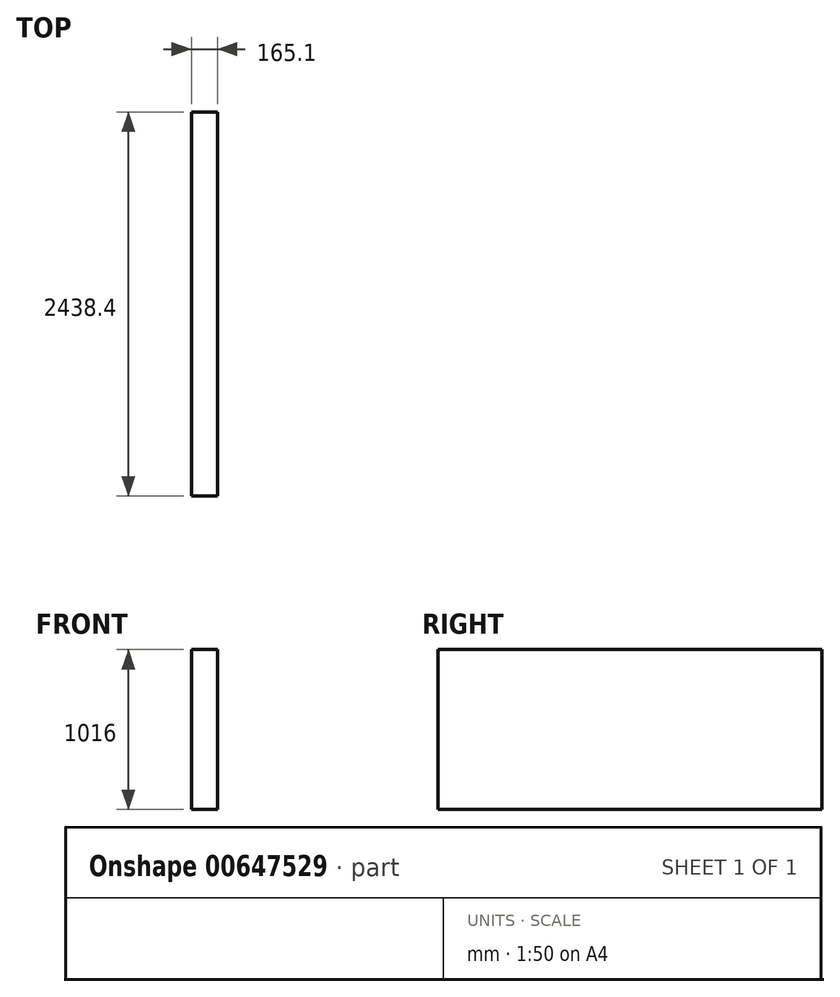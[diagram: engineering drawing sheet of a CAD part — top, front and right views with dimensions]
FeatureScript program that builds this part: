
annotation { "Feature Type Name" : "Feature", "Feature Type Description" : "" }
export const myFeature = defineFeature(function(context is Context, id is Id, definition is map)
    precondition{}
    {
        {
            var Q0;
            Q0=qCreatedBy(makeId("Front.planeOp"),FACE);
            var sketch = newSketch(context, id + "F0", { "sketchPlane" : qUnion([Q0])});
            skLineSegment(sketch, "E0.bottom", {"start": v(0, 0) * mm, "end": v(-165.1, 0) * mm});
            skLineSegment(sketch, "E0.top", {"start": v(0, 1016) * mm, "end": v(-165.1, 1016) * mm});
            skLineSegment(sketch, "E0.left", {"start": v(0, 0) * mm, "end": v(0, 1016) * mm});
            skLineSegment(sketch, "E0.right", {"start": v(-165.1, 0) * mm, "end": v(-165.1, 1016) * mm});
            skSolve(sketch);
        }
        {
            var Q0;
            Q0=makeQuery(id+"F0.imprint","IMPRINT",FACE,{"disambiguationData":[TD([[makeQuery(id+"F0.imprint","IMPRINT",EDGE,{"derivedFrom":sQuery(id+"F0.wireOp",EDGE,"E0.bottom")}),-1.0]])]});
            extrude(context, id + "F1", {"entities" : qUnion([Q0]), "depth" : 2438.4 * mm, "offsetDistance" : 25.4 * mm});
        }
    });
